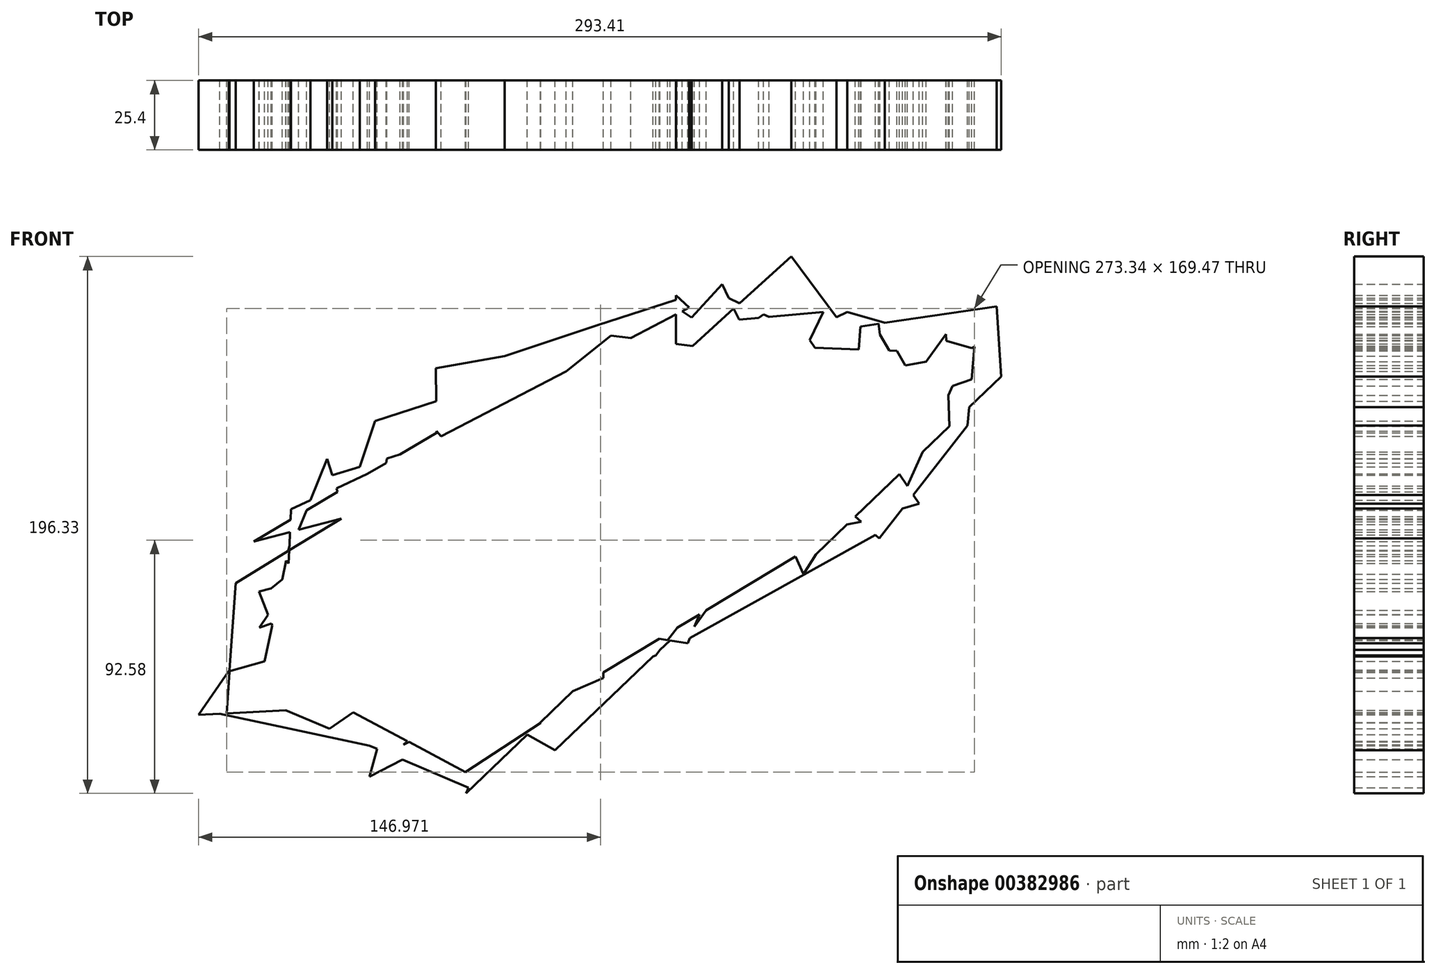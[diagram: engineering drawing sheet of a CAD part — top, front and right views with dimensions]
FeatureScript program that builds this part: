
annotation { "Feature Type Name" : "Feature", "Feature Type Description" : "" }
export const myFeature = defineFeature(function(context is Context, id is Id, definition is map)
    precondition{}
    {
        {
            var Q0;
            Q0=qCreatedBy(makeId("Front.planeOp"),FACE);
            var sketch = newSketch(context, id + "F0", { "sketchPlane" : qUnion([Q0])});
            skLineSegment(sketch, "E0", {"start": v(-91.67, 17.4) * mm, "end": v(41.88, 57.92) * mm});
            skLineSegment(sketch, "E1", {"start": v(-16.82, 65.38) * mm, "end": v(-13.52, 12.58) * mm});
            skLineSegment(sketch, "E2", {"start": v(-63.64, -3.53) * mm, "end": v(21.43, 88.95) * mm});
            skLineSegment(sketch, "E3", {"start": v(-27.7, 46.74) * mm, "end": v(37.92, 16.22) * mm});
            skLineSegment(sketch, "E4", {"start": v(25.06, 67.9) * mm, "end": v(-37.4, 0) * mm});
            skLineSegment(sketch, "E5", {"start": v(-66.94, -8.11) * mm, "end": v(22.28, 18.96) * mm});
            skLineSegment(sketch, "E6", {"start": v(-53.42, 49.54) * mm, "end": v(-26.7, -17.6) * mm});
            skLineSegment(sketch, "E7", {"start": v(-22.75, 59.71) * mm, "end": v(-25.72, -7.42) * mm});
            skLineSegment(sketch, "E8", {"start": v(-103.87, -24.7) * mm, "end": v(34.62, 39.67) * mm});
            skLineSegment(sketch, "E9", {"start": v(-85.08, 36.11) * mm, "end": v(-28.36, -23.03) * mm});
            skLineSegment(sketch, "E10", {"start": v(-33.63, 58.88) * mm, "end": v(-96.17, -21.13) * mm});
            skLineSegment(sketch, "E11", {"start": v(-66.28, 42.86) * mm, "end": v(53.75, 35.96) * mm});
            skLineSegment(sketch, "E12", {"start": v(-23.74, 68.33) * mm, "end": v(12.86, 0) * mm});
            skLineSegment(sketch, "E13", {"start": v(22.1, 81.56) * mm, "end": v(-51.11, -48.06) * mm});
            skLineSegment(sketch, "E14", {"start": v(-107.5, -41.91) * mm, "end": v(42.87, 24.9) * mm});
            skLineSegment(sketch, "E15", {"start": v(-111.79, 3.67) * mm, "end": v(-27.7, -43.85) * mm});
            skLineSegment(sketch, "E16", {"start": v(-14.84, 73.54) * mm, "end": v(-134.87, -22.78) * mm});
            skLineSegment(sketch, "E17", {"start": v(-122.34, 0) * mm, "end": v(-86.4, -57.26) * mm});
            skLineSegment(sketch, "E18", {"start": v(-122.67, -60.47) * mm, "end": v(41.32, -10.7) * mm});
            skLineSegment(sketch, "E19", {"start": v(30.34, 68.44) * mm, "end": v(-40.89, -65.55) * mm});
            skLineSegment(sketch, "E20", {"start": v(-52.1, 21.56) * mm, "end": v(17.72, -17.86) * mm});
            skLineSegment(sketch, "E21", {"start": v(48.14, 55.78) * mm, "end": v(8.24, -43.13) * mm});
            skLineSegment(sketch, "E22", {"start": v(-32.98, 71.27) * mm, "end": v(57.05, 59.71) * mm});
            skLineSegment(sketch, "E23", {"start": v(42.54, 68.67) * mm, "end": v(42.87, 24.9) * mm});
            skLineSegment(sketch, "E24", {"start": v(-134.87, -22.78) * mm, "end": v(-122.67, -65.55) * mm});
            skLineSegment(sketch, "E25", {"start": v(-122.67, -65.55) * mm, "end": v(42.87, -15.31) * mm});
            skLineSegment(sketch, "E26", {"start": v(-94.28, -6.22) * mm, "end": v(-109.15, -65.55) * mm});
            skLineSegment(sketch, "E27", {"start": v(-134.87, -55.33) * mm, "end": v(-57.05, 11.56) * mm});
            skLineSegment(sketch, "E28", {"start": v(-111.05, -3.66) * mm, "end": v(-37.4, -80.45) * mm});
            skLineSegment(sketch, "E29", {"start": v(-8.16, 56.78) * mm, "end": v(-62, -91.43) * mm});
            skLineSegment(sketch, "E30", {"start": v(-95.63, -80.04) * mm, "end": v(34.62, -19.49) * mm});
            skLineSegment(sketch, "E31", {"start": v(-92.6, -47.38) * mm, "end": v(-79.8, -81.4) * mm});
            skLineSegment(sketch, "E32", {"start": v(-95.63, -80.04) * mm, "end": v(-48.73, -38.03) * mm});
            skLineSegment(sketch, "E33", {"start": v(48.14, 18.56) * mm, "end": v(-5.44, -50) * mm});
            skLineSegment(sketch, "E34", {"start": v(-86.4, -92.2) * mm, "end": v(48.14, -10.94) * mm});
            skLineSegment(sketch, "E35", {"start": v(-128.6, -60.47) * mm, "end": v(-71.9, -90.62) * mm});
            skLineSegment(sketch, "E36", {"start": v(-6.6, 77.9) * mm, "end": v(0, 55.07) * mm});
            skLineSegment(sketch, "E37", {"start": v(-24.73, 73.32) * mm, "end": v(12.86, 85.5) * mm});
            skLineSegment(sketch, "E38", {"start": v(3.96, 87.87) * mm, "end": v(3.96, 58.38) * mm});
            skLineSegment(sketch, "E39", {"start": v(0, 87.87) * mm, "end": v(10.84, 77.9) * mm});
            skLineSegment(sketch, "E40", {"start": v(0, 82.88) * mm, "end": v(27.7, 63.48) * mm});
            skPoint(sketch, "E40.startSnap0", {"position": v(5.42, 82.88) * mm});
            skLineSegment(sketch, "E41", {"start": v(-0.99, 55.77) * mm, "end": v(48.14, 100.3) * mm});
            skLineSegment(sketch, "E42", {"start": v(17.15, 95.96) * mm, "end": v(36.26, 56.22) * mm});
            skLineSegment(sketch, "E43", {"start": v(7.81, 56.28) * mm, "end": v(56.06, 92.35) * mm});
            skLineSegment(sketch, "E44", {"start": v(10.84, 88.95) * mm, "end": v(59.68, 66.36) * mm});
            skLineSegment(sketch, "E45", {"start": v(62.98, 88.95) * mm, "end": v(42.7, 46.79) * mm});
            skLineSegment(sketch, "E46", {"start": v(21.76, 74.87) * mm, "end": v(57.82, 78.22) * mm});
            skLineSegment(sketch, "E47", {"start": v(-99.91, 33.48) * mm, "end": v(-112.45, -29.16) * mm});
            skLineSegment(sketch, "E48", {"start": v(-167.18, -27.16) * mm, "end": v(-53.42, 42.12) * mm});
            skLineSegment(sketch, "E49", {"start": v(-104.86, 41.94) * mm, "end": v(-125.3, -19.68) * mm});
            skLineSegment(sketch, "E50", {"start": v(-119.04, 13.45) * mm, "end": v(8.81, 79.76) * mm});
            skLineSegment(sketch, "E51", {"start": v(-53.42, 65.93) * mm, "end": v(-68.9, 19.25) * mm});
            skLineSegment(sketch, "E52", {"start": v(-114.42, 35.56) * mm, "end": v(-53.42, 55.3) * mm});
            skLineSegment(sketch, "E53", {"start": v(-83.76, 57.6) * mm, "end": v(-83.46, 18.47) * mm});
            skLineSegment(sketch, "E54", {"start": v(-104.86, 41.94) * mm, "end": v(-75.84, 64.5) * mm});
            skLineSegment(sketch, "E55", {"start": v(-83.76, 57.6) * mm, "end": v(-53.42, 62.97) * mm});
            skLineSegment(sketch, "E56", {"start": v(-125.3, 17.4) * mm, "end": v(-91.67, 27.65) * mm});
            skLineSegment(sketch, "E57", {"start": v(-112.12, 52.71) * mm, "end": v(-134.9, -3.79) * mm});
            skLineSegment(sketch, "E58", {"start": v(-150.37, -5.82) * mm, "end": v(-105.42, 5.98) * mm});
            skLineSegment(sketch, "E59", {"start": v(-135.53, 35.56) * mm, "end": v(-137.84, -19.68) * mm});
            skLineSegment(sketch, "E60", {"start": v(-146.4, -24.79) * mm, "end": v(-104.89, 8.62) * mm});
            skLineSegment(sketch, "E61", {"start": v(-143.11, -7.35) * mm, "end": v(-126.96, -26.15) * mm});
            skLineSegment(sketch, "E62", {"start": v(-105.42, 20.52) * mm, "end": v(-136.76, 5.98) * mm});
            skLineSegment(sketch, "E63", {"start": v(-150.37, -5.82) * mm, "end": v(-75.18, 38.97) * mm});
            skLineSegment(sketch, "E64", {"start": v(-123.51, 24.46) * mm, "end": v(-110.23, -18.1) * mm});
            skLineSegment(sketch, "E65", {"start": v(-160.26, -27.14) * mm, "end": v(-95.25, -10.07) * mm});
            skLineSegment(sketch, "E66", {"start": v(-157.95, 0) * mm, "end": v(-128.27, -75.28) * mm});
            skLineSegment(sketch, "E67", {"start": v(-142.12, -77.3) * mm, "end": v(-106.68, -55.72) * mm});
            skLineSegment(sketch, "E68", {"start": v(-142.13, -40.13) * mm, "end": v(-119.04, -32.8) * mm});
            skLineSegment(sketch, "E69", {"start": v(-58.6, 62.05) * mm, "end": v(-24.73, 73.32) * mm});
            skLineSegment(sketch, "E70", {"start": v(-36.27, 77.9) * mm, "end": v(-50.45, -5.82) * mm});
            skLineSegment(sketch, "E71", {"start": v(5.42, -5.82) * mm, "end": v(7.95, -12.34) * mm});
            skLineSegment(sketch, "E72", {"start": v(6.6, -12.6) * mm, "end": v(86.06, 26.5) * mm});
            skLineSegment(sketch, "E73", {"start": v(30.67, 26.33) * mm, "end": v(51.44, -19.68) * mm});
            skLineSegment(sketch, "E74", {"start": v(77.82, 64.01) * mm, "end": v(21.43, -5.82) * mm});
            skLineSegment(sketch, "E75", {"start": v(30.67, 39.52) * mm, "end": v(79.47, -5.82) * mm});
            skLineSegment(sketch, "E76", {"start": v(52.84, 67.87) * mm, "end": v(98.27, 0) * mm});
            skLineSegment(sketch, "E77", {"start": v(52.1, -13.32) * mm, "end": v(125.96, 57.6) * mm});
            skLineSegment(sketch, "E78", {"start": v(-128.27, -78.22) * mm, "end": v(-53.66, -25.6) * mm});
            skLineSegment(sketch, "E79", {"start": v(-140.45, -66.74) * mm, "end": v(-64.47, -98.87) * mm});
            skLineSegment(sketch, "E80", {"start": v(-98.3, -57.09) * mm, "end": v(-109.4, -96.31) * mm});
            skLineSegment(sketch, "E81", {"start": v(-115.5, -95.58) * mm, "end": v(-47, -60.28) * mm});
            skLineSegment(sketch, "E82", {"start": v(-64.81, -79.17) * mm, "end": v(-74.88, -102.96) * mm});
            skLineSegment(sketch, "E83", {"start": v(-97.75, -106.26) * mm, "end": v(-36.19, -66.03) * mm});
            skLineSegment(sketch, "E84", {"start": v(-15.05, -42.58) * mm, "end": v(-86.58, -111.18) * mm});
            skLineSegment(sketch, "E85", {"start": v(-63.68, -68.88) * mm, "end": v(-36.46, -84.27) * mm});
            skLineSegment(sketch, "E86", {"start": v(10.18, -33.87) * mm, "end": v(-50.02, -91.6) * mm});
            skLineSegment(sketch, "E87", {"start": v(-65.86, -74.32) * mm, "end": v(4.85, -43.85) * mm});
            skLineSegment(sketch, "E88", {"start": v(-49.5, -39.37) * mm, "end": v(-24.82, -78.83) * mm});
            skLineSegment(sketch, "E89", {"start": v(-22.6, -37.99) * mm, "end": v(-22.6, -78.75) * mm});
            skLineSegment(sketch, "E90", {"start": v(-14.28, -39.47) * mm, "end": v(14, -43.85) * mm});
            skLineSegment(sketch, "E91", {"start": v(25.65, -16.02) * mm, "end": v(-5.96, -60.36) * mm});
            skLineSegment(sketch, "E92", {"start": v(2.08, -45) * mm, "end": v(89.7, 3.86) * mm});
            skLineSegment(sketch, "E93", {"start": v(81.94, 32.12) * mm, "end": v(32.58, -46.18) * mm});
            skLineSegment(sketch, "E94", {"start": v(52.1, -2.43) * mm, "end": v(81.1, 3.32) * mm});
            skLineSegment(sketch, "E95", {"start": v(74.73, 2.59) * mm, "end": v(101.76, 10.8) * mm});
            skLineSegment(sketch, "E96", {"start": v(75.28, -8.34) * mm, "end": v(111.88, 38.27) * mm});
            skLineSegment(sketch, "E97", {"start": v(78.6, 55.28) * mm, "end": v(42.28, 14.85) * mm});
            skLineSegment(sketch, "E98", {"start": v(43.12, 56.13) * mm, "end": v(98.3, 41.56) * mm});
            skLineSegment(sketch, "E99", {"start": v(78.05, 73.98) * mm, "end": v(78.05, 11.6) * mm});
            skLineSegment(sketch, "E100", {"start": v(53.1, 65.11) * mm, "end": v(84.7, 63.98) * mm});
            skLineSegment(sketch, "E101", {"start": v(71.4, 72.9) * mm, "end": v(67.8, 20.83) * mm});
            skLineSegment(sketch, "E102", {"start": v(70.01, 55.58) * mm, "end": v(99.13, 60.65) * mm});
            skLineSegment(sketch, "E103", {"start": v(78.05, 73.98) * mm, "end": v(81.94, 36.8) * mm});
            skLineSegment(sketch, "E104", {"start": v(76.67, 73.03) * mm, "end": v(97.74, 37.24) * mm});
            skLineSegment(sketch, "E105", {"start": v(73.06, 40.1) * mm, "end": v(122.97, 57.28) * mm});
            skLineSegment(sketch, "E106", {"start": v(69.74, 76.57) * mm, "end": v(92.2, 15.67) * mm});
            skLineSegment(sketch, "E107", {"start": v(87.48, 12.37) * mm, "end": v(112.16, 66.91) * mm});
            skLineSegment(sketch, "E108", {"start": v(84.7, 63.98) * mm, "end": v(103.01, 32.12) * mm});
            skLineSegment(sketch, "E109", {"start": v(51.43, 71) * mm, "end": v(84.7, 86.7) * mm});
            skLineSegment(sketch, "E110", {"start": v(30.08, 119.75) * mm, "end": v(104.67, 20.38) * mm});
            skLineSegment(sketch, "E111", {"start": v(112.16, 83) * mm, "end": v(63.91, 16.94) * mm});
            skLineSegment(sketch, "E112", {"start": v(71.4, 72.9) * mm, "end": v(129.63, 81.38) * mm});
            skLineSegment(sketch, "E113", {"start": v(115.49, 93.38) * mm, "end": v(108.28, 10.33) * mm});
            skLineSegment(sketch, "E114", {"start": v(60.86, 79.83) * mm, "end": v(115.49, 63.98) * mm});
            skLineSegment(sketch, "E115", {"start": v(102.18, 84) * mm, "end": v(104.19, 28.47) * mm});
            skLineSegment(sketch, "E116", {"start": v(83.6, 53.68) * mm, "end": v(131.85, 72.9) * mm});
            skLineSegment(sketch, "E117", {"start": v(119.92, 101.04) * mm, "end": v(123.25, 47.93) * mm});
            skLineSegment(sketch, "E118", {"start": v(-162.63, -42.08) * mm, "end": v(-124.09, -29.02) * mm});
            skLineSegment(sketch, "E119", {"start": v(-156.25, -10.02) * mm, "end": v(-160.41, -70.56) * mm});
            skLineSegment(sketch, "E120", {"start": v(-174.28, -57.37) * mm, "end": v(-52.27, -23.54) * mm});
            skLineSegment(sketch, "E121", {"start": v(-137.32, -7.35) * mm, "end": v(-157.92, -103.67) * mm});
            skLineSegment(sketch, "E122", {"start": v(-188.42, -70.05) * mm, "end": v(-52.32, -63.02) * mm});
            skLineSegment(sketch, "E123", {"start": v(-163.74, -49.34) * mm, "end": v(-131.57, -79.43) * mm});
            skLineSegment(sketch, "E124", {"start": v(-141.66, -27.66) * mm, "end": v(-179, -81.19) * mm});
            skLineSegment(sketch, "E125", {"start": v(-177.05, -65.66) * mm, "end": v(-108.02, -80.45) * mm});
            skSolve(sketch);
        }
        {
            var Q0;
            Q0 = qSketchRegion(id + "F0", true);
            extrude(context, id + "F1", {"entities" : qUnion([Q0]), "depth" : 25.4 * mm});
        }
    });
